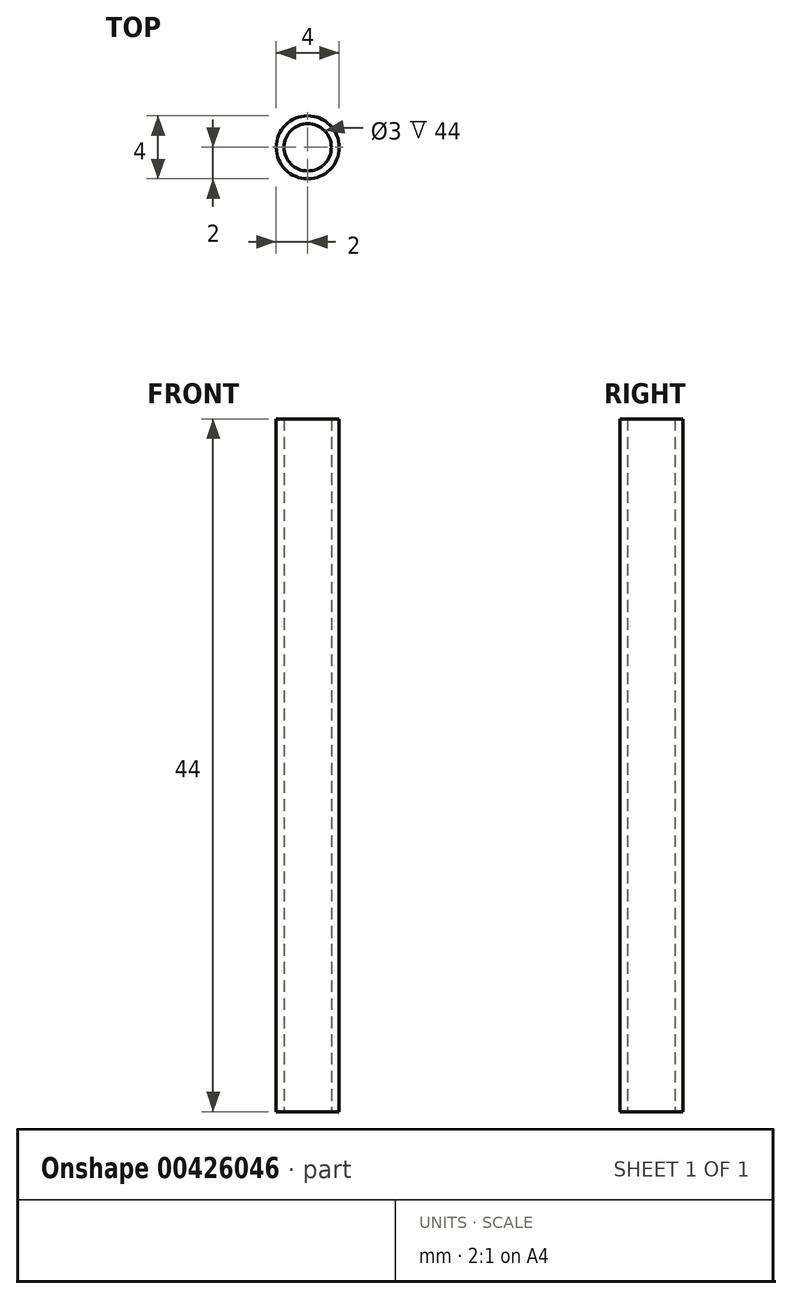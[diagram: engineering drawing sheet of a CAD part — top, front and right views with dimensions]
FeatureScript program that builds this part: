
annotation { "Feature Type Name" : "Feature", "Feature Type Description" : "" }
export const myFeature = defineFeature(function(context is Context, id is Id, definition is map)
    precondition{}
    {
        {
            var Q0;
            Q0=qCreatedBy(makeId("Top.planeOp"),FACE);
            var sketch = newSketch(context, id + "F0", { "sketchPlane" : qUnion([Q0])});
            skCircle(sketch, "E0", {"center": v(0, 0) * mm, "radius": 1.5 * mm});
            skCircle(sketch, "E1", {"center": v(0, 0) * mm, "radius": 2 * mm});
            skSolve(sketch);
        }
        {
            var Q0;
            Q0=makeQuery(id+"F0.imprint","IMPRINT",FACE,{"disambiguationData":[TD([[makeQuery(id+"F0.imprint","IMPRINT",EDGE,{"derivedFrom":sQuery(id+"F0.wireOp",EDGE,"E0")}),-1.0]])]});
            extrude(context, id + "F1", {"entities" : qUnion([Q0]), "depth" : 22 * mm, "hasSecondDirection" : true, "secondDirectionOppositeDirection" : true, "secondDirectionDepth" : 22 * mm});
        }
    });
